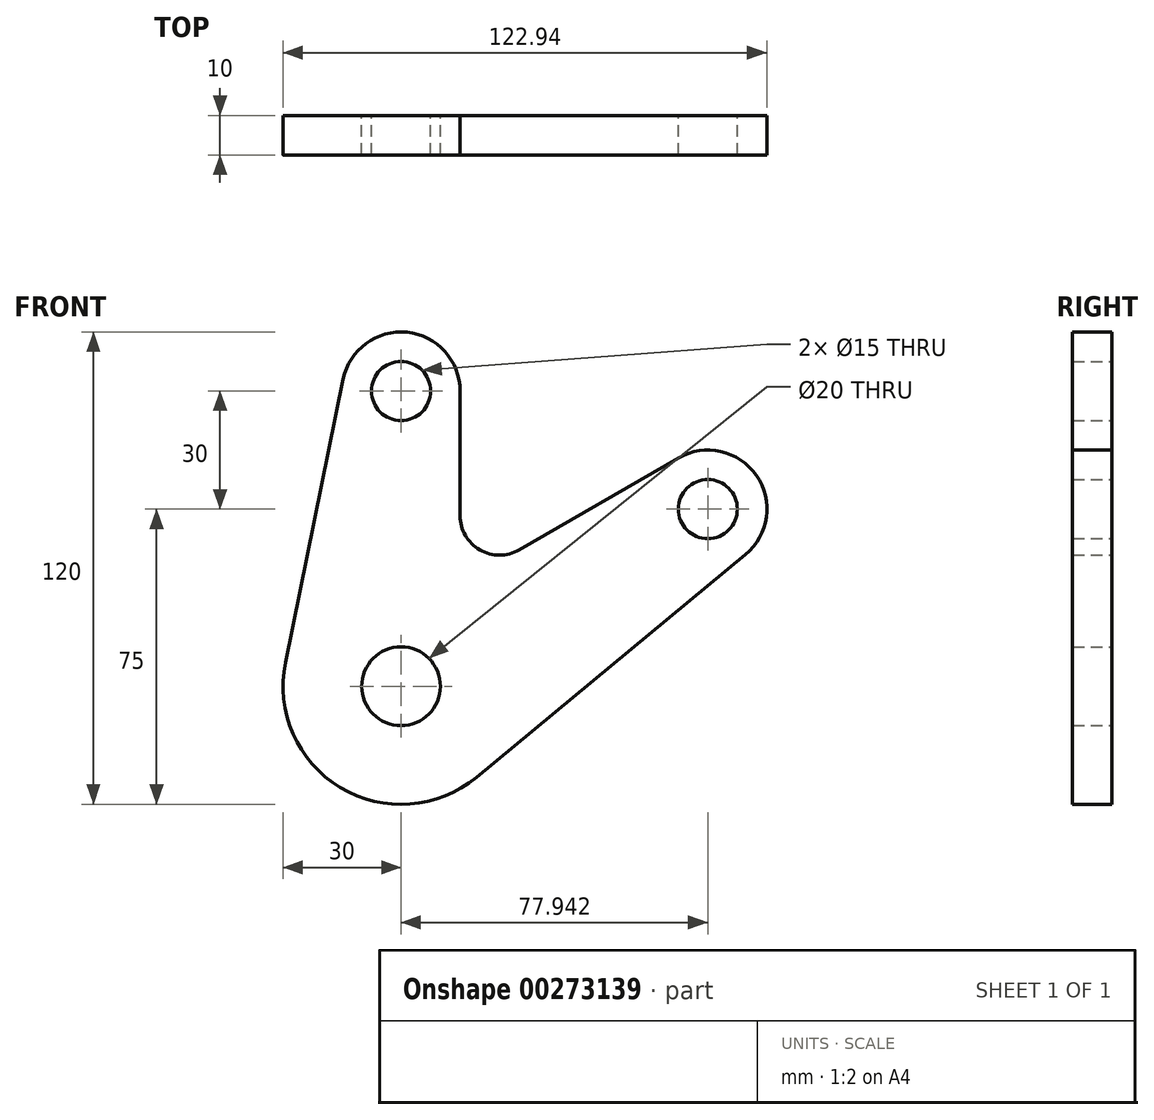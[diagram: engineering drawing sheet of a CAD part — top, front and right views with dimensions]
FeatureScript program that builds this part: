
annotation { "Feature Type Name" : "Feature", "Feature Type Description" : "" }
export const myFeature = defineFeature(function(context is Context, id is Id, definition is map)
    precondition{}
    {
        {
            var Q0;
            Q0=qCreatedBy(makeId("Front.planeOp"),FACE);
            var sketch = newSketch(context, id + "F0", { "sketchPlane" : qUnion([Q0])});
            skCircle(sketch, "E0", {"center": v(0, 0) * mm, "radius": 10 * mm});
            skCircle(sketch, "E1", {"center": v(0, 75) * mm, "radius": 7.5 * mm});
            skCircle(sketch, "E2", {"center": v(77.94, 45) * mm, "radius": 7.5 * mm});
            skLineSegment(sketch, "E3", {"start": v(-14.7, 78) * mm, "end": v(-29.4, 6) * mm});
            skLineSegment(sketch, "E4", {"start": v(19.12, -23.12) * mm, "end": v(87.5, 33.44) * mm});
            skArc(sketch, "E5", {"start": v(-29.4, 6) * mm, "mid": v(-15.44, -25.72) * mm, "end": v(19.12, -23.12) * mm});
            skLineSegment(sketch, "E6", {"start": v(15, 75) * mm, "end": v(15, 43.3) * mm});
            skLineSegment(sketch, "E7", {"start": v(70.44, 58) * mm, "end": v(30, 34.64) * mm});
            skArc(sketch, "E8", {"start": v(15, 75) * mm, "mid": v(1.5, 89.92) * mm, "end": v(-14.7, 78) * mm});
            skArc(sketch, "E9", {"start": v(15, 43.3) * mm, "mid": v(20, 34.64) * mm, "end": v(30, 34.64) * mm});
            skArc(sketch, "E10", {"start": v(87.5, 33.44) * mm, "mid": v(90.26, 53.56) * mm, "end": v(70.44, 58) * mm});
            skLineSegment(sketch, "E11", {"start": v(0, 75) * mm, "end": v(0, 0) * mm});
            skLineSegment(sketch, "E12", {"start": v(0, 0) * mm, "end": v(77.94, 45) * mm});
            skSolve(sketch);
        }
        {
            var Q0;
            Q0 = qSketchRegion(id + "F0", true);
            extrude(context, id + "F1", {"entities" : qUnion([Q0]), "depth" : 10 * mm});
        }
    });
